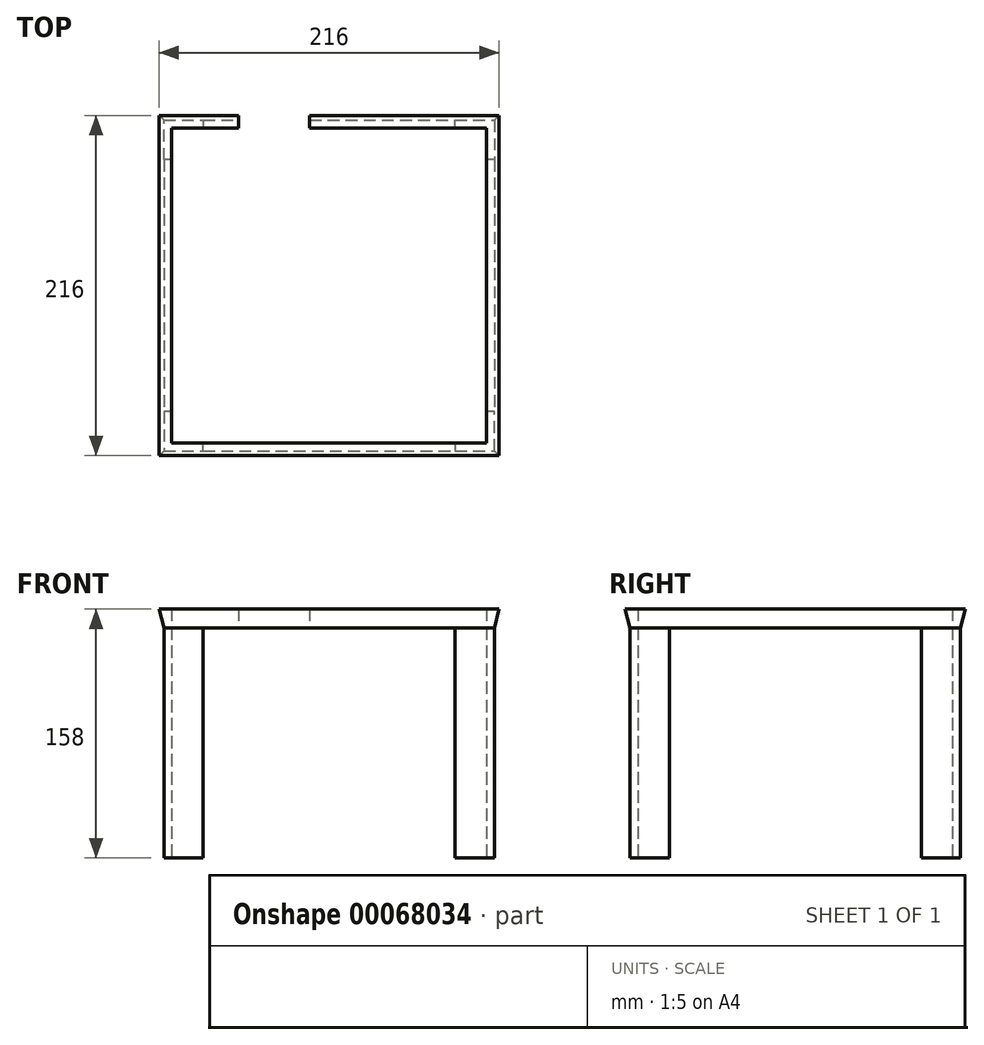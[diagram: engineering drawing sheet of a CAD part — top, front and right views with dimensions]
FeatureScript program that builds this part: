
annotation { "Feature Type Name" : "Feature", "Feature Type Description" : "" }
export const myFeature = defineFeature(function(context is Context, id is Id, definition is map)
    precondition{}
    {
        {
            var Q0;
            Q0=qCreatedBy(makeId("Top.planeOp"),FACE);
            var sketch = newSketch(context, id + "F0", { "sketchPlane" : qUnion([Q0])});
            skLineSegment(sketch, "E0", {"start": v(0, 0) * mm, "end": v(25, 0) * mm});
            skLineSegment(sketch, "E1", {"start": v(25, 0) * mm, "end": v(25, -5) * mm});
            skLineSegment(sketch, "E2", {"start": v(25, -5) * mm, "end": v(5, -5) * mm});
            skLineSegment(sketch, "E3", {"start": v(5, -5) * mm, "end": v(5, -25) * mm});
            skLineSegment(sketch, "E4", {"start": v(5, -25) * mm, "end": v(0, -25) * mm});
            skLineSegment(sketch, "E5", {"start": v(0, -25) * mm, "end": v(0, 0) * mm});
            skLineSegment(sketch, "E6", {"start": v(185, 0) * mm, "end": v(210, 0) * mm});
            skLineSegment(sketch, "E7", {"start": v(210, 0) * mm, "end": v(210, -25) * mm});
            skLineSegment(sketch, "E8", {"start": v(210, -25) * mm, "end": v(205, -25) * mm});
            skLineSegment(sketch, "E9", {"start": v(205, -25) * mm, "end": v(205, -5) * mm});
            skLineSegment(sketch, "E10", {"start": v(205, -5) * mm, "end": v(185, -5) * mm});
            skLineSegment(sketch, "E11", {"start": v(185, -5) * mm, "end": v(185, 0) * mm});
            skLineSegment(sketch, "E12", {"start": v(0, -185) * mm, "end": v(0, -210) * mm});
            skLineSegment(sketch, "E13", {"start": v(0, -210) * mm, "end": v(25, -210) * mm});
            skLineSegment(sketch, "E14", {"start": v(25, -210) * mm, "end": v(25, -205) * mm});
            skLineSegment(sketch, "E15", {"start": v(25, -205) * mm, "end": v(5, -205) * mm});
            skLineSegment(sketch, "E16", {"start": v(5, -205) * mm, "end": v(5, -185) * mm});
            skLineSegment(sketch, "E17", {"start": v(5, -185) * mm, "end": v(0, -185) * mm});
            skLineSegment(sketch, "E18", {"start": v(210, -210) * mm, "end": v(210, -185) * mm});
            skLineSegment(sketch, "E19", {"start": v(210, -185) * mm, "end": v(205, -185) * mm});
            skLineSegment(sketch, "E20", {"start": v(205, -185) * mm, "end": v(205, -205) * mm});
            skLineSegment(sketch, "E21", {"start": v(205, -205) * mm, "end": v(185, -205) * mm});
            skLineSegment(sketch, "E22", {"start": v(185, -205) * mm, "end": v(185, -210) * mm});
            skLineSegment(sketch, "E23", {"start": v(185, -210) * mm, "end": v(210, -210) * mm});
            skSolve(sketch);
        }
        {
            var Q0;
            Q0 = qSketchRegion(id + "F0", true);
            extrude(context, id + "F1", {"entities" : qUnion([Q0]), "depth" : 146 * mm});
        }
        {
            var Q0;
            Q0=makeQuery(id+"F1.opExtrude","CAP_FACE",FACE,{"disambiguationData":[OSD([sQuery(id+"F0.wireOp",EDGE,"E12"),sQuery(id+"F0.wireOp",EDGE,"E13"),sQuery(id+"F0.wireOp",EDGE,"E14"),sQuery(id+"F0.wireOp",EDGE,"E15"),sQuery(id+"F0.wireOp",EDGE,"E16"),sQuery(id+"F0.wireOp",EDGE,"E17")])],"isStart":false});
            var sketch = newSketch(context, id + "F2", { "sketchPlane" : qUnion([Q0])});
            skLineSegment(sketch, "E24.bottom", {"start": v(0, 0) * mm, "end": v(210, 0) * mm});
            skLineSegment(sketch, "E24.top", {"start": v(0, -210) * mm, "end": v(210, -210) * mm});
            skLineSegment(sketch, "E24.left", {"start": v(0, 0) * mm, "end": v(0, -210) * mm});
            skLineSegment(sketch, "E24.right", {"start": v(210, 0) * mm, "end": v(210, -210) * mm});
            skSolve(sketch);
        }
        {
            var Q0;
            {var subQ3=sQuery(id+"F2.wireOp",EDGE,"E24.bottom");Q0=makeQuery(id+"F2.imprint","IMPRINT",FACE,{"disambiguationData":[TD([[makeQuery(id+"F2.imprint","IMPRINT",EDGE,{"derivedFrom":subQ3}),-1.0]])]});}
            cPlane(context, id + "F3", {"entities" : qUnion([Q0]), "cplaneType" : CPlaneType.OFFSET, "offset" : 12 * mm, "width" : 150 * mm, "height" : 150 * mm});
        }
        {
            var Q0;
            Q0=qCreatedBy(id+"F3.planeOp",FACE);
            var sketch = newSketch(context, id + "F4", { "sketchPlane" : qUnion([Q0])});
            skLineSegment(sketch, "E25.bottom", {"start": v(-3, 3) * mm, "end": v(213, 3) * mm});
            skLineSegment(sketch, "E25.top", {"start": v(-3, -213) * mm, "end": v(213, -213) * mm});
            skLineSegment(sketch, "E25.left", {"start": v(-3, 3) * mm, "end": v(-3, -213) * mm});
            skLineSegment(sketch, "E25.right", {"start": v(213, 3) * mm, "end": v(213, -213) * mm});
            skSolve(sketch);
        }
        {
            var Q0;
            Q0 = qSketchRegion(id + "F4", true);
            var Q1;
            Q1 = qSketchRegion(id + "F2", true);
            loft(context, id + "F5", {"operationType" : NewBodyOperationType.ADD, "sheetProfilesArray" : [{ "sheetProfileEntities" : qUnion([Q0]) }, { "sheetProfileEntities" : qUnion([Q1]) }]});
        }
        {
            var Q0;
            Q0=makeQuery(id+"F5.opLoft","CAP_FACE",FACE,{"disambiguationData":[OSD([makeQuery(id+"F4.imprint","IMPRINT",FACE,{"disambiguationData":[TD([[makeQuery(id+"F4.imprint","IMPRINT",EDGE,{"derivedFrom":sQuery(id+"F4.wireOp",EDGE,"E25.bottom")}),-1.0]])]})])],"isStart":true});
            var sketch = newSketch(context, id + "F6", { "sketchPlane" : qUnion([Q0])});
            skLineSegment(sketch, "E26.bottom", {"start": v(5, -5) * mm, "end": v(205, -5) * mm});
            skLineSegment(sketch, "E26.top", {"start": v(5, -205) * mm, "end": v(205, -205) * mm});
            skLineSegment(sketch, "E26.left", {"start": v(5, -5) * mm, "end": v(5, -205) * mm});
            skLineSegment(sketch, "E26.right", {"start": v(205, -5) * mm, "end": v(205, -205) * mm});
            skSolve(sketch);
        }
        {
            var Q0;
            Q0 = qSketchRegion(id + "F6", true);
            extrude(context, id + "F7", {"entities" : qUnion([Q0]), "operationType" : NewBodyOperationType.REMOVE, "oppositeDirection" : true, "depth" : 12 * mm});
        }
        {
            var Q0;
            Q0=qCreatedBy(makeId("Top.planeOp"),FACE);
            var sketch = newSketch(context, id + "F8", { "sketchPlane" : qUnion([Q0])});
            skLineSegment(sketch, "E27.bottom", {"start": v(47.5, -5) * mm, "end": v(92.5, -5) * mm});
            skLineSegment(sketch, "E27.top", {"start": v(47.5, 20) * mm, "end": v(92.5, 20) * mm});
            skLineSegment(sketch, "E27.left", {"start": v(47.5, -5) * mm, "end": v(47.5, 20) * mm});
            skLineSegment(sketch, "E27.right", {"start": v(92.5, -5) * mm, "end": v(92.5, 20) * mm});
            skSolve(sketch);
        }
        {
            var Q0;
            Q0=makeQuery(id+"F8.imprint","IMPRINT",FACE,{"disambiguationData":[TD([[makeQuery(id+"F8.imprint","IMPRINT",EDGE,{"derivedFrom":sQuery(id+"F8.wireOp",EDGE,"E27.bottom")}),1.0]])]});
            extrude(context, id + "F9", {"entities" : qUnion([Q0]), "operationType" : NewBodyOperationType.REMOVE, "depth" : 180 * mm});
        }
    });
